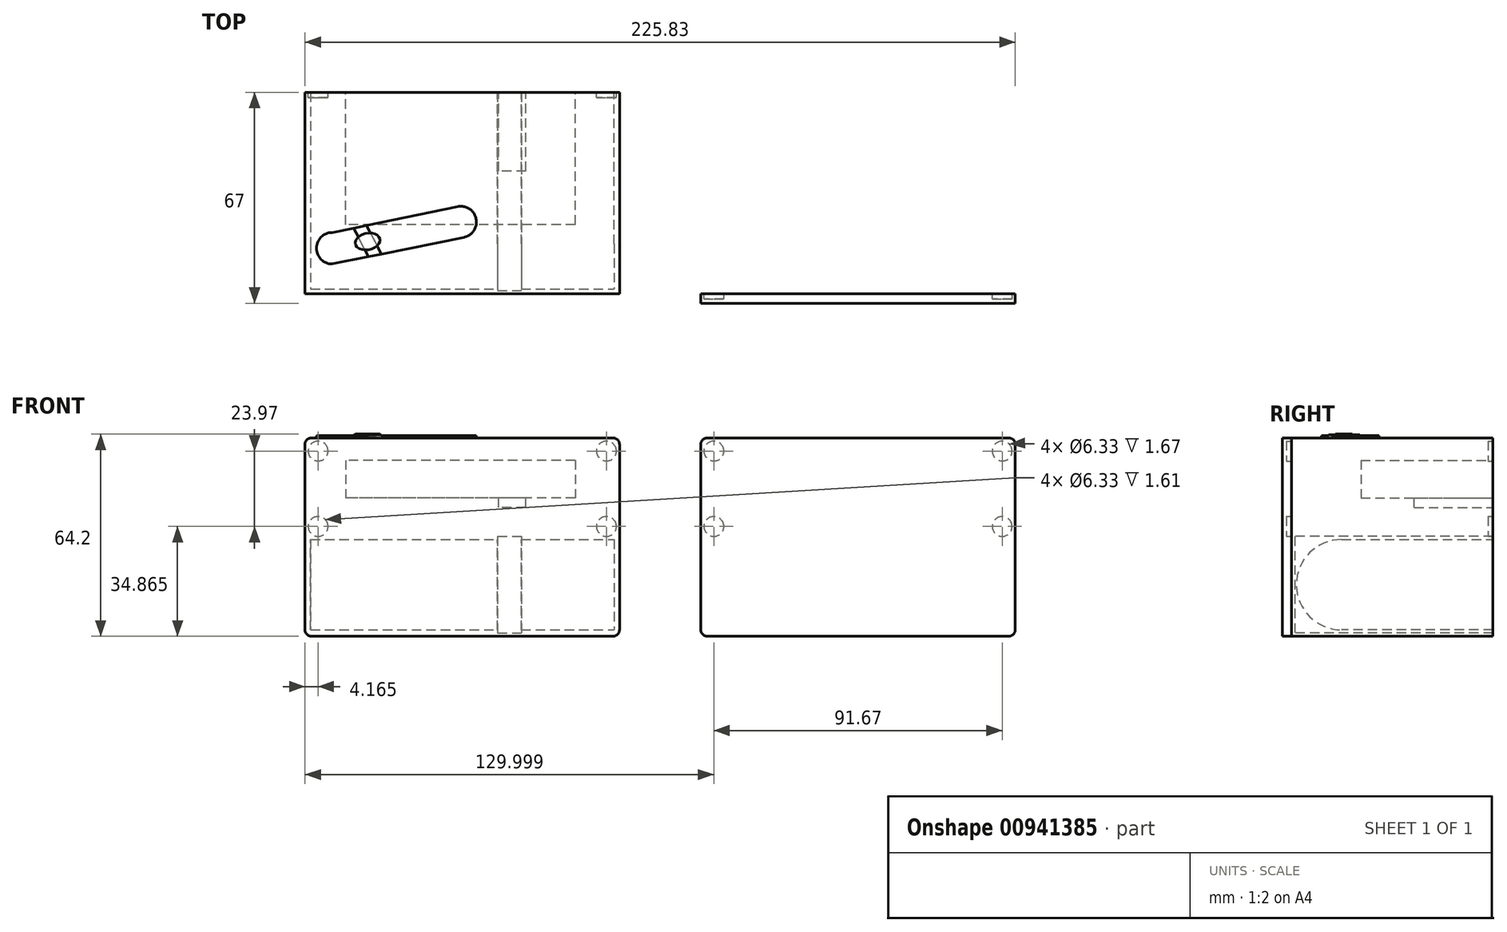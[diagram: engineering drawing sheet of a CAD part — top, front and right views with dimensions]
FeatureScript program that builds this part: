
annotation { "Feature Type Name" : "Feature", "Feature Type Description" : "" }
export const myFeature = defineFeature(function(context is Context, id is Id, definition is map)
    precondition{}
    {
        {
            var Q0;
            Q0=qCreatedBy(makeId("Top.planeOp"),FACE);
            var sketch = newSketch(context, id + "F0", { "sketchPlane" : qUnion([Q0])});
            skLineSegment(sketch, "E0.bottom", {"start": v(-100, 64) * mm, "end": v(0, 64) * mm});
            skLineSegment(sketch, "E0.top", {"start": v(-100, 0) * mm, "end": v(0, 0) * mm});
            skLineSegment(sketch, "E0.left", {"start": v(-100, 64) * mm, "end": v(-100, 0) * mm});
            skLineSegment(sketch, "E0.right", {"start": v(0, 64) * mm, "end": v(0, 0) * mm});
            skSolve(sketch);
        }
        {
            var Q0;
            Q0=qSketchRegion(id+"F0",true);
            extrude(context, id + "F1", {"entities" : qUnion([Q0]), "depth" : 63 * mm, "offsetDistance" : 25 * mm});
        }
        {
            var Q0;
            Q0=makeQuery(id+"F1.opExtrude","SWEPT_FACE",FACE,{"disambiguationData":[OSD([sQuery(id+"F0.wireOp",EDGE,"E0.right")])]});
            var sketch = newSketch(context, id + "F2", { "sketchPlane" : qUnion([Q0])});
            skCircle(sketch, "E1", {"center": v(15.85, 16.35) * mm, "radius": 14.35 * mm});
            skCircle(sketch, "E2", {"center": v(47.85, 16.35) * mm, "radius": 14.35 * mm});
            skLineSegment(sketch, "E3", {"start": v(15.85, 30.7) * mm, "end": v(47.85, 30.7) * mm});
            skLineSegment(sketch, "E4", {"start": v(15.85, 2) * mm, "end": v(47.85, 2) * mm});
            skLineSegment(sketch, "E5", {"start": v(47.85, 30.7) * mm, "end": v(64, 30.7) * mm});
            skLineSegment(sketch, "E6", {"start": v(64, 30.7) * mm, "end": v(64, 2) * mm});
            skLineSegment(sketch, "E7", {"start": v(64, 2) * mm, "end": v(47.85, 2) * mm});
            skSolve(sketch);
        }
        {
            var Q0;
            Q0=qSketchRegion(id+"F2",true);
            extrude(context, id + "F3", {"entities" : qUnion([Q0]), "operationType" : NewBodyOperationType.REMOVE, "endBound" : BoundingType.UP_TO_NEXT, "oppositeDirection" : true, "depth" : 186.6 * mm, "hasOffset" : true, "offsetDistance" : 1.75 * mm, "hasSecondDirection" : true, "secondDirectionOppositeDirection" : true, "secondDirectionDepth" : 1.75 * mm, "hasSecondDirectionOffset" : true, "secondDirectionOffsetDistance" : 2 * mm, "secondDirectionOffsetOppositeDirection" : true});
        }
        {
            var Q0;
            Q0=makeQuery(id+"F1.opExtrude","SWEPT_FACE",FACE,{"disambiguationData":[OSD([sQuery(id+"F0.wireOp",EDGE,"E0.top")])]});
            var sketch = newSketch(context, id + "F4", { "sketchPlane" : qUnion([Q0])});
            skLineSegment(sketch, "E8.bottom", {"start": v(-38.75, 31.7) * mm, "end": v(-31.25, 31.7) * mm});
            skLineSegment(sketch, "E8.top", {"start": v(-38.75, 1) * mm, "end": v(-31.25, 1) * mm});
            skLineSegment(sketch, "E8.left", {"start": v(-38.75, 31.7) * mm, "end": v(-38.75, 1) * mm});
            skLineSegment(sketch, "E8.right", {"start": v(-31.25, 31.7) * mm, "end": v(-31.25, 1) * mm});
            skLineSegment(sketch, "E9", {"start": v(0, 0) * mm, "end": v(-66.11, 0) * mm, "construction": true});
            skSolve(sketch);
        }
        {
            var Q0;
            Q0=qSketchRegion(id+"F4",true);
            var Q1;
            Q1=makeQuery(id+"F1.opExtrude","SWEPT_FACE",FACE,{"disambiguationData":[OSD([sQuery(id+"F0.wireOp",EDGE,"E0.bottom")])]});
            var Q2;
            Q2=makeQuery(id+"F1.opExtrude","SWEPT_BODY",BODY,{"disambiguationData":[OSD([sQuery(id+"F0.wireOp",EDGE,"E0.bottom"),sQuery(id+"F0.wireOp",EDGE,"E0.top"),sQuery(id+"F0.wireOp",EDGE,"E0.left"),sQuery(id+"F0.wireOp",EDGE,"E0.right")])]});
            extrude(context, id + "F5", {"entities" : qUnion([Q0]), "operationType" : NewBodyOperationType.REMOVE, "endBound" : BoundingType.UP_TO_SURFACE, "oppositeDirection" : true, "depth" : 25 * mm, "endBoundEntityFace" : qUnion([Q1]), "endBoundEntityBody" : qUnion([Q2]), "offsetDistance" : 1 * mm, "hasSecondDirection" : true, "secondDirectionOppositeDirection" : true, "secondDirectionDepth" : 1 * mm, "hasSecondDirectionOffset" : true, "secondDirectionOffsetDistance" : 1 * mm});
        }
        {
            var Q0;
            Q0=makeQuery(id+"F1.opExtrude","SWEPT_FACE",FACE,{"disambiguationData":[OSD([sQuery(id+"F0.wireOp",EDGE,"E0.bottom")])]});
            var sketch = newSketch(context, id + "F6", { "sketchPlane" : qUnion([Q0])});
            skLineSegment(sketch, "E10.bottom", {"start": v(14.07, 55.92) * mm, "end": v(87.07, 55.92) * mm});
            skLineSegment(sketch, "E10.top", {"start": v(14.07, 43.92) * mm, "end": v(87.07, 43.92) * mm});
            skLineSegment(sketch, "E10.left", {"start": v(14.07, 55.92) * mm, "end": v(14.07, 43.92) * mm});
            skLineSegment(sketch, "E10.right", {"start": v(87.07, 55.92) * mm, "end": v(87.07, 43.92) * mm});
            skLineSegment(sketch, "E11.bottom", {"start": v(29.77, 40.92) * mm, "end": v(38.37, 40.92) * mm});
            skLineSegment(sketch, "E11.left", {"start": v(29.77, 40.92) * mm, "end": v(29.77, 43.92) * mm});
            skLineSegment(sketch, "E11.right", {"start": v(38.37, 40.92) * mm, "end": v(38.37, 43.92) * mm});
            skSolve(sketch);
        }
        {
            var Q0;
            Q0=makeQuery(id+"F6.imprint","IMPRINT",FACE,{"disambiguationData":[TD([[makeQuery(id+"F6.imprint","IMPRINT",EDGE,{"derivedFrom":sQuery(id+"F6.wireOp",EDGE,"E10.bottom")}),-1.0]])]});
            extrude(context, id + "F7", {"entities" : qUnion([Q0]), "operationType" : NewBodyOperationType.REMOVE, "oppositeDirection" : true, "depth" : 42 * mm, "offsetDistance" : 25 * mm});
        }
        {
            var Q0;
            Q0=makeQuery(id+"F6.imprint","IMPRINT",FACE,{"disambiguationData":[TD([[makeQuery(id+"F6.imprint","IMPRINT",EDGE,{"derivedFrom":sQuery(id+"F6.wireOp",EDGE,"E11.bottom")}),1.0]])]});
            extrude(context, id + "F8", {"entities" : qUnion([Q0]), "operationType" : NewBodyOperationType.REMOVE, "oppositeDirection" : true, "depth" : 25 * mm, "offsetDistance" : 25 * mm});
        }
        {
            var Q0;
            Q0=qCreatedBy(makeId("Front.planeOp"),FACE);
            var sketch = newSketch(context, id + "F9", { "sketchPlane" : qUnion([Q0])});
            skLineSegment(sketch, "E12.bottom", {"start": v(125.83, 63) * mm, "end": v(25.83, 63) * mm});
            skLineSegment(sketch, "E12.top", {"start": v(125.83, 0) * mm, "end": v(25.83, 0) * mm});
            skLineSegment(sketch, "E12.left", {"start": v(125.83, 63) * mm, "end": v(125.83, 0) * mm});
            skLineSegment(sketch, "E12.right", {"start": v(25.83, 63) * mm, "end": v(25.83, 0) * mm});
            skSolve(sketch);
        }
        {
            var Q0;
            Q0=makeQuery(id+"F9.imprint","IMPRINT",FACE,{"disambiguationData":[TD([[makeQuery(id+"F9.imprint","IMPRINT",EDGE,{"derivedFrom":sQuery(id+"F9.wireOp",EDGE,"E12.bottom")}),1.0]])]});
            extrude(context, id + "F10", {"entities" : qUnion([Q0]), "depth" : 3 * mm, "offsetDistance" : 25 * mm});
        }
        {
            var Q0;
            Q0=makeQuery(id+"F6.imprint","IMPRINT",FACE,{"disambiguationData":[TD([[makeQuery(id+"F6.imprint","IMPRINT",EDGE,{"derivedFrom":sQuery(id+"F6.wireOp",EDGE,"E10.bottom")}),1.0]])]});
            var sketch = newSketch(context, id + "F11", { "sketchPlane" : qUnion([Q0])});
            skCircle(sketch, "E13", {"center": v(95.84, 58.84) * mm, "radius": 3.17 * mm});
            skCircle(sketch, "E14", {"center": v(95.84, 34.87) * mm, "radius": 3.17 * mm});
            skCircle(sketch, "E15", {"center": v(4.16, 58.84) * mm, "radius": 3.17 * mm});
            skCircle(sketch, "E16", {"center": v(4.17, 34.87) * mm, "radius": 3.17 * mm});
            skSolve(sketch);
        }
        {
            var Q0;
            Q0=qSketchRegion(id+"F11",true);
            extrude(context, id + "F12", {"entities" : qUnion([Q0]), "operationType" : NewBodyOperationType.REMOVE, "oppositeDirection" : true, "depth" : 1.61 * mm, "offsetDistance" : 25 * mm});
        }
        {
            var Q0;
            Q0=makeQuery(id+"F10.opExtrude","CAP_FACE",FACE,{"disambiguationData":[OSD([sQuery(id+"F9.wireOp",EDGE,"E12.bottom"),sQuery(id+"F9.wireOp",EDGE,"E12.top"),sQuery(id+"F9.wireOp",EDGE,"E12.left"),sQuery(id+"F9.wireOp",EDGE,"E12.right")])],"isStart":true});
            var sketch = newSketch(context, id + "F13", { "sketchPlane" : qUnion([Q0])});
            skCircle(sketch, "E17", {"center": v(-30, 34.87) * mm, "radius": 3.17 * mm});
            skCircle(sketch, "E18", {"center": v(-30, 58.83) * mm, "radius": 3.17 * mm});
            skCircle(sketch, "E19", {"center": v(-121.67, 58.84) * mm, "radius": 3.17 * mm});
            skCircle(sketch, "E20", {"center": v(-121.67, 34.87) * mm, "radius": 3.17 * mm});
            skSolve(sketch);
        }
        {
            var Q0;
            Q0=qSketchRegion(id+"F13",true);
            extrude(context, id + "F14", {"entities" : qUnion([Q0]), "operationType" : NewBodyOperationType.REMOVE, "oppositeDirection" : true, "depth" : 1.67 * mm, "offsetDistance" : 25 * mm});
        }
        {
            var Q0;
            Q0=makeQuery(id+"F1.opExtrude","CAP_EDGE",EDGE,{"disambiguationData":[OSD([sQuery(id+"F0.wireOp",EDGE,"E0.right")])],"isStart":false});
            var Q1;
            Q1=makeQuery(id+"F1.opExtrude","CAP_EDGE",EDGE,{"disambiguationData":[OSD([sQuery(id+"F0.wireOp",EDGE,"E0.right")])],"isStart":true});
            var Q2;
            Q2=makeQuery(id+"F1.opExtrude","CAP_EDGE",EDGE,{"disambiguationData":[OSD([sQuery(id+"F0.wireOp",EDGE,"E0.left")])],"isStart":true});
            var Q3;
            Q3=makeQuery(id+"F1.opExtrude","CAP_EDGE",EDGE,{"disambiguationData":[OSD([sQuery(id+"F0.wireOp",EDGE,"E0.left")])],"isStart":false});
            var Q4;
            Q4=makeQuery(id+"F10.opExtrude","SWEPT_EDGE",EDGE,{"disambiguationData":[OSD([sQuery(id+"F9.wireOp",EDGE,"E12.bottom"),sQuery(id+"F9.wireOp",EDGE,"E12.left")])]});
            var Q5;
            Q5=makeQuery(id+"F10.opExtrude","SWEPT_EDGE",EDGE,{"disambiguationData":[OSD([sQuery(id+"F9.wireOp",EDGE,"E12.top"),sQuery(id+"F9.wireOp",EDGE,"E12.left")])]});
            var Q6;
            Q6=makeQuery(id+"F10.opExtrude","SWEPT_EDGE",EDGE,{"disambiguationData":[OSD([sQuery(id+"F9.wireOp",EDGE,"E12.top"),sQuery(id+"F9.wireOp",EDGE,"E12.right")])]});
            var Q7;
            Q7=makeQuery(id+"F10.opExtrude","SWEPT_EDGE",EDGE,{"disambiguationData":[OSD([sQuery(id+"F9.wireOp",EDGE,"E12.bottom"),sQuery(id+"F9.wireOp",EDGE,"E12.right")])]});
            fillet(context, id + "F15", {"entities" : qUnion([Q0, Q1, Q2, Q3, Q4, Q5, Q6, Q7]), "radius" : 2 * mm, "tangentPropagation" : true, "allowEdgeOverflow" : false});
        }
        {
            var Q0;
            Q0=makeQuery(id+"F1.opExtrude","CAP_FACE",FACE,{"disambiguationData":[OSD([sQuery(id+"F0.wireOp",EDGE,"E0.bottom"),sQuery(id+"F0.wireOp",EDGE,"E0.top"),sQuery(id+"F0.wireOp",EDGE,"E0.left"),sQuery(id+"F0.wireOp",EDGE,"E0.right")])],"isStart":false});
            var sketch = newSketch(context, id + "F16", { "sketchPlane" : qUnion([Q0])});
            skCircle(sketch, "E21", {"center": v(-91.34, 14.47) * mm, "radius": 5 * mm});
            skCircle(sketch, "E22", {"center": v(-50.5, 22.82) * mm, "radius": 5 * mm});
            skLineSegment(sketch, "E23", {"start": v(-91.34, 19.47) * mm, "end": v(-51.52, 27.71) * mm});
            skLineSegment(sketch, "E24", {"start": v(-91.34, 9.47) * mm, "end": v(-49.51, 17.91) * mm});
            skEllipse(sketch, "E25", {"center": v(-80.06, 16.62) * mm, "majorRadius": 2.5 * mm, "minorRadius": 2 * mm, "majorAxis": v(0.48, -0.88)});
            skLineSegment(sketch, "E26", {"start": v(-79.8, 11.8) * mm, "end": v(-84.53, 20.88) * mm});
            skLineSegment(sketch, "E27", {"start": v(-80.46, 21.72) * mm, "end": v(-75.72, 12.62) * mm});
            skSolve(sketch);
        }
        {
            var Q0;
            {var subQ0=sQuery(id+"F16.wireOp",EDGE,"E24");var subQ1=sQuery(id+"F16.wireOp",EDGE,"E21");var subQ2=makeQuery(id+"F16.imprint","INTERSECT",VERTEX,{"disambiguationData":[OD(0.0)],"derivedFrom":[subQ1,subQ0]});Q0=makeQuery(id+"F16.imprint","IMPRINT",FACE,{"disambiguationData":[TD([[makeQuery(id+"F16.imprint","IMPRINT",EDGE,{"disambiguationData":[TD([[subQ2,-1.0]])],"derivedFrom":subQ1}),1.0]])]});}
            var Q1;
            {var subQ0=sQuery(id+"F16.wireOp",EDGE,"E22");var subQ1=makeQuery(id+"F16.imprint","INTERSECT",VERTEX,{"derivedFrom":[subQ0,sQuery(id+"F16.wireOp",EDGE,"E23")]});Q1=makeQuery(id+"F16.imprint","IMPRINT",FACE,{"disambiguationData":[TD([[makeQuery(id+"F16.imprint","IMPRINT",EDGE,{"disambiguationData":[TD([[subQ1,-1.0]])],"derivedFrom":subQ0}),1.0]])]});}
            var Q2;
            {var subQ0=sQuery(id+"F16.wireOp",EDGE,"E21");var subQ1=makeQuery(id+"F16.imprint","INTERSECT",VERTEX,{"derivedFrom":[subQ0,sQuery(id+"F16.wireOp",EDGE,"E23")]});Q2=makeQuery(id+"F16.imprint","IMPRINT",FACE,{"disambiguationData":[TD([[makeQuery(id+"F16.imprint","IMPRINT",EDGE,{"disambiguationData":[TD([[subQ1,-1.0]])],"derivedFrom":subQ0}),1.0]])]});}
            var Q3;
            {var subQ4=sQuery(id+"F16.wireOp",EDGE,"E21");var subQ6=sQuery(id+"F16.wireOp",EDGE,"E23");var subQ7=makeQuery(id+"F16.imprint","INTERSECT",VERTEX,{"derivedFrom":[subQ4,subQ6]});Q3=makeQuery(id+"F16.imprint","IMPRINT",FACE,{"disambiguationData":[TD([[makeQuery(id+"F16.imprint","IMPRINT",EDGE,{"disambiguationData":[TD([[subQ7,1.0]])],"derivedFrom":subQ4}),-1.0]])]});}
            var Q4;
            {var subQ1=sQuery(id+"F16.wireOp",EDGE,"E23");var subQ5=sQuery(id+"F16.wireOp",EDGE,"E22");var subQ8=makeQuery(id+"F16.imprint","INTERSECT",VERTEX,{"derivedFrom":[subQ5,subQ1]});Q4=makeQuery(id+"F16.imprint","IMPRINT",FACE,{"disambiguationData":[TD([[makeQuery(id+"F16.imprint","IMPRINT",EDGE,{"disambiguationData":[TD([[subQ8,-1.0]])],"derivedFrom":subQ5}),-1.0]])]});}
            extrude(context, id + "F17", {"entities" : qUnion([Q0, Q1, Q2, Q3, Q4]), "operationType" : NewBodyOperationType.ADD, "depth" : .8 * mm, "offsetDistance" : 25 * mm});
        }
        {
            var Q0;
            {var subQ0=sQuery(id+"F16.wireOp",EDGE,"E26");var subQ1=sQuery(id+"F16.wireOp",EDGE,"E23");var subQ2=makeQuery(id+"F16.imprint","INTERSECT",VERTEX,{"derivedFrom":[subQ1,subQ0]});Q0=makeQuery(id+"F16.imprint","IMPRINT",FACE,{"disambiguationData":[TD([[makeQuery(id+"F16.imprint","IMPRINT",EDGE,{"disambiguationData":[TD([[subQ2,-1.0]])],"derivedFrom":subQ1}),-1.0]])]});}
            var Q1;
            {var subQ0=sQuery(id+"F16.wireOp",EDGE,"E26");var subQ1=sQuery(id+"F16.wireOp",EDGE,"E24");var subQ2=makeQuery(id+"F16.imprint","INTERSECT",VERTEX,{"derivedFrom":[subQ1,subQ0]});Q1=makeQuery(id+"F16.imprint","IMPRINT",FACE,{"disambiguationData":[TD([[makeQuery(id+"F16.imprint","IMPRINT",EDGE,{"disambiguationData":[TD([[subQ2,-1.0]])],"derivedFrom":subQ1}),1.0]])]});}
            var Q2;
            {var subQ0=sQuery(id+"F16.wireOp",EDGE,"E25");var subQ1=makeQuery(id+"F16.imprint","INTERSECT",VERTEX,{"derivedFrom":[subQ0,sQuery(id+"F16.wireOp",EDGE,"E26")]});Q2=makeQuery(id+"F16.imprint","IMPRINT",FACE,{"disambiguationData":[TD([[makeQuery(id+"F16.imprint","IMPRINT",EDGE,{"disambiguationData":[TD([[subQ1,1.0]])],"derivedFrom":subQ0}),1.0]])]});}
            extrude(context, id + "F18", {"entities" : qUnion([Q0, Q1, Q2]), "operationType" : NewBodyOperationType.ADD, "depth" : 1 * mm, "offsetDistance" : 25 * mm});
        }
        {
            var Q0;
            Q0=makeQuery(id+"F18.opExtrude","CAP_FACE",FACE,{"disambiguationData":[OSD([sQuery(id+"F16.wireOp",EDGE,"E23"),sQuery(id+"F16.wireOp",EDGE,"E24"),sQuery(id+"F16.wireOp",EDGE,"E26"),sQuery(id+"F16.wireOp",EDGE,"E27")])],"isStart":false});
            var sketch = newSketch(context, id + "F19", { "sketchPlane" : qUnion([Q0])});
            skEllipse(sketch, "E28", {"center": v(-80.1, 16.63) * mm, "majorRadius": 3.98 * mm, "minorRadius": 2.61 * mm, "majorAxis": v(0.98, 0.2)});
            skSolve(sketch);
        }
        {
            var Q0;
            Q0=qSketchRegion(id+"F19",true);
            extrude(context, id + "F20", {"entities" : qUnion([Q0]), "operationType" : NewBodyOperationType.ADD, "depth" : .2 * mm, "offsetDistance" : 25 * mm});
        }
    });
